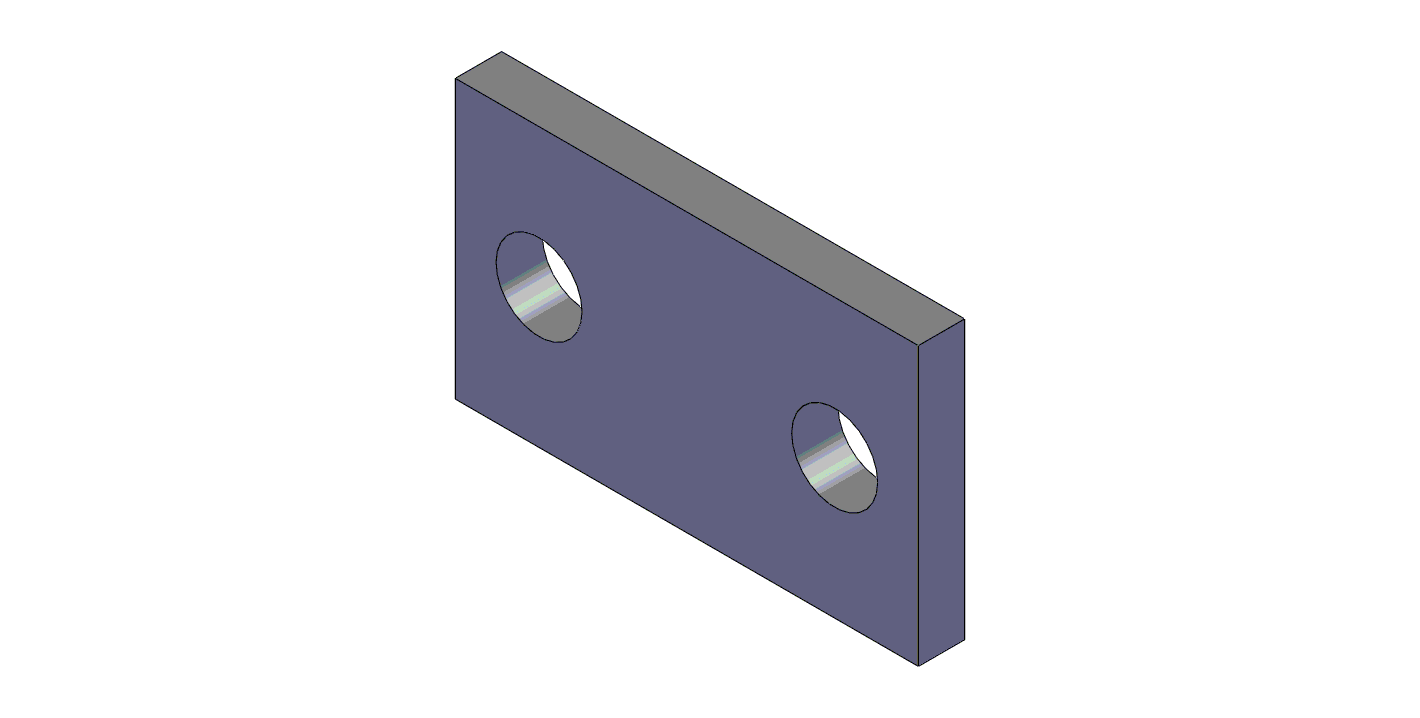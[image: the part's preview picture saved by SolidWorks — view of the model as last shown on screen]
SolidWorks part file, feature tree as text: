
SOLIDWORKS PART (.sldprt)
format: sldprt  version: not decoded by parser v0  size: 148,992 bytes
history: native  units: mm
features: sketch x3, material x1, extrude x1, hole x1 (+12 scaffold rows collapsed)
feature tree (18):
  scaffold x12  (default folders/planes/origin — collapsed)
  material  "Material <not specified>"
  sketch  "Sketch1"  dims[D1=15.875mm D2=9.525mm]
  extrude  "Boss-Extrude1"  Depth=1.5875mm
  hole  "#4 Clearance Hole1"  Diameter=2.9464mm Depth=1.5875mm
  sketch  "Sketch3"  dims[D1=10.1346mm]
  sketch  "Sketch2"  dims[hole-wizard template sketch: 60 standard entries collapsed; hole parameters kept: c18.Thru Hole Depth=1.5875mm]
decode coverage: 5 of 5 modeling features carry decoded parameters
note: ~ marks probable driven/reference dimensions
note: suppression state not decoded; provenance and decode notes live in map.json
